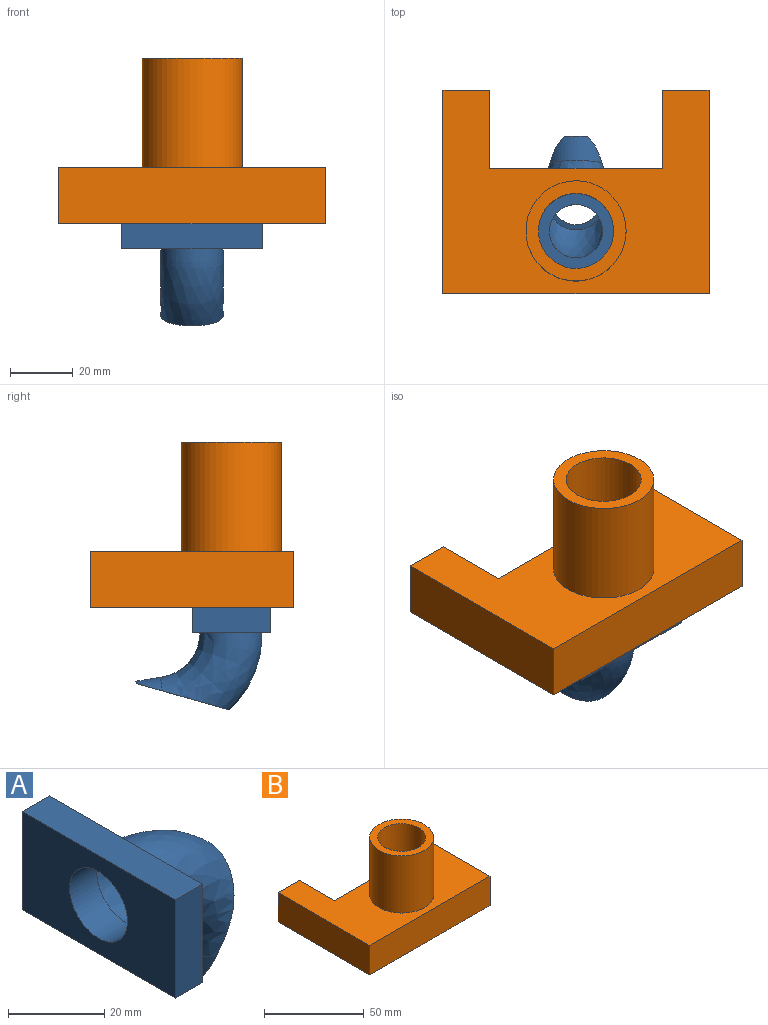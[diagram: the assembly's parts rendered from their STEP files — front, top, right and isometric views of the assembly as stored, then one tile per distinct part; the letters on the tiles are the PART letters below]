
ASSEMBLY  parts=2 mates=1
PART A: 12 faces, bbox 44.8x47.8x45.7 mm
  f0: plane 7.47x0.71mm, normal (0.16,0,-0.99), area 3.6mm2, adj f1,f11
  f1: cylinder r=10mm len=16.6mm, axis (0.16,0,-0.99), area 107.7mm2, adj f0,f2,f11
  f2: bspline ~40x34mm, area 1601mm2, adj f1,f10,f11
  f3: cylinder r=8.5mm len=12.83mm, axis (0.16,0,-0.99), area 59.4mm2, adj f11
  f4: plane 25x8mm, normal (0,-1,0), area 200mm2, adj f5,f7,f9,f10
  f5: plane 45x8mm, normal (0,0,-1), area 360mm2, adj f4,f6,f9,f10
  f6: plane 25x8mm, normal (0,1,0), area 200mm2, adj f5,f7,f9,f10
  f7: plane 45x8mm, normal (0,0,1), area 360mm2, adj f4,f6,f9,f10
  f8: cylinder r=8.5mm len=17mm, axis (1,0,0), area 427.3mm2, adj f9
  f9: plane 45x25mm, normal (-1,0,0), area 898mm2, adj f4,f5,f6,f7,f8
  f10: plane 47.78x27.78mm, normal (1,0,0), area 810.8mm2, adj f2,f4,f5,f6,f7
  f11: plane 31.32x21.46mm, normal (0.96,0,-0.27), area 137.3mm2, adj f0,f1,f2,f3
PART B: 13 faces, bbox 85x65x53 mm
  f0: plane 65x18mm, normal (1,0,0), area 1170mm2, adj f1,f7,f8,f9
  f1: plane 18x15mm, normal (0,1,0), area 270mm2, adj f0,f2,f8,f9
  f2: plane 25x18mm, normal (-1,0,0), area 450mm2, adj f1,f3,f8,f9
  f3: plane 55x18mm, normal (0,1,0), area 990mm2, adj f2,f4,f8,f9
  f4: plane 25x18mm, normal (1,0,0), area 450mm2, adj f3,f5,f8,f9
  f5: plane 18x15mm, normal (0,1,0), area 270mm2, adj f4,f6,f8,f9
  f6: plane 65x18mm, normal (-1,0,0), area 1170mm2, adj f5,f7,f8,f9
  f7: plane 85x18mm, normal (0,-1,0), area 1530mm2, adj f0,f6,f8,f9
  f8: plane 85x65mm, normal (0,0,1), area 3345.8mm2, adj f0,f1,f2,f3,f4,f5,f6,f7
  f9: plane 85x65mm, normal (0,0,-1), area 3697.6mm2, adj f0,f1,f2,f3,f4,f5,f6,f7
  f10: cylinder r=16mm len=35mm, axis (0,0,-1), area 3518.6mm2, adj f8,f11
  f11: plane 32x32mm, normal (0,0,1), area 351.9mm2, adj f10,f12
  f12: cylinder r=12mm len=53mm, axis (0,0,1), area 3996.1mm2, adj f9,f11
PLACE A rot(axis=(0.58,0.58,-0.58),120deg) t=(-13.6,5.52,4.31)mm
PLACE B t=(-13.6,18.02,12.31)mm fixed
MATE fastened B.f10 <-> A.f8  axis (0,0,1) through (-13.6,5.52,12.31)mm
